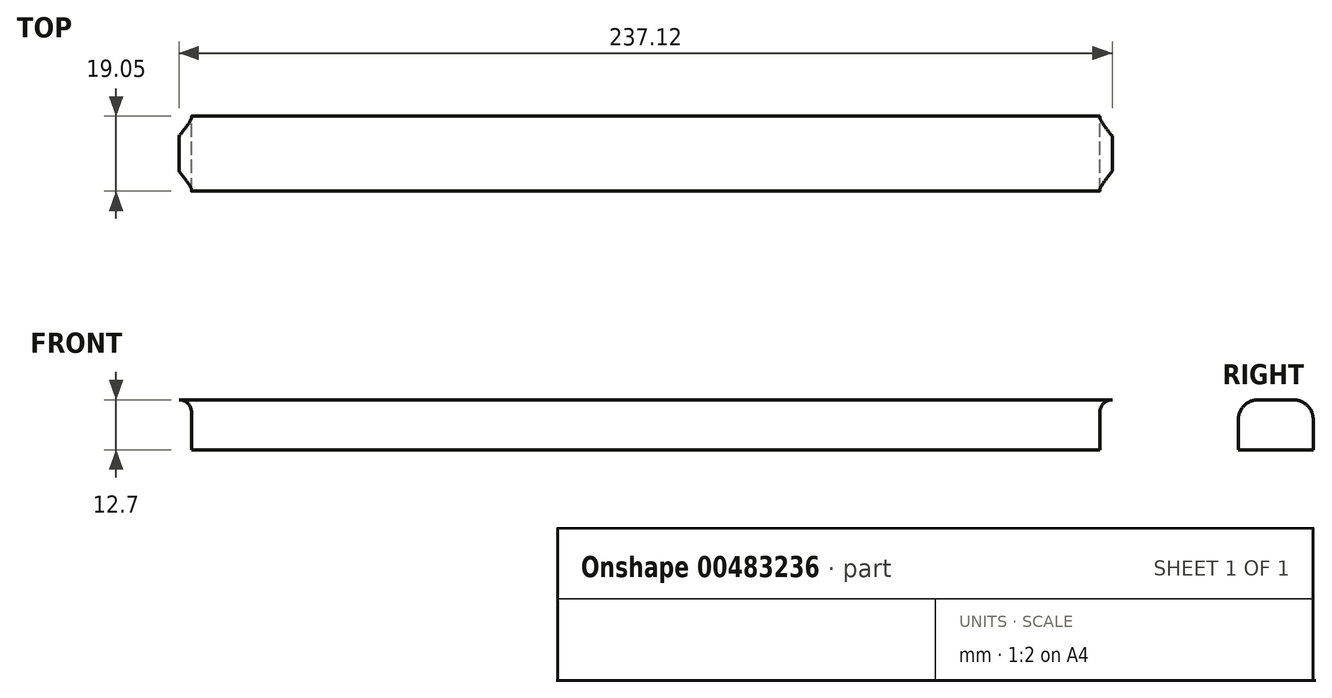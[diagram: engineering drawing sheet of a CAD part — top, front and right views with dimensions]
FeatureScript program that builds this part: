
annotation { "Feature Type Name" : "Feature", "Feature Type Description" : "" }
export const myFeature = defineFeature(function(context is Context, id is Id, definition is map)
    precondition{}
    {
        {
            var Q0;
            Q0=qCreatedBy(makeId("Front.planeOp"),FACE);
            var sketch = newSketch(context, id + "F0", { "sketchPlane" : qUnion([Q0])});
            skLineSegment(sketch, "E0.bottom", {"start": v(118.56, 6.35) * mm, "end": v(-118.56, 6.35) * mm});
            skLineSegment(sketch, "E0.top", {"start": v(115.39, -6.35) * mm, "end": v(-115.39, -6.35) * mm});
            skPoint(sketch, "E0.middle", {"position": v(0, 0) * mm});
            skLineSegment(sketch, "E1", {"start": v(-115.39, 3.18) * mm, "end": v(-115.39, -6.35) * mm});
            skLineSegment(sketch, "E2", {"start": v(115.39, 3.17) * mm, "end": v(115.39, -6.35) * mm});
            skArc(sketch, "E3", {"start": v(118.56, 6.35) * mm, "mid": v(116.32, 5.42) * mm, "end": v(115.39, 3.17) * mm});
            skPoint(sketch, "E4.orphan", {"position": v(118.56, -6.35) * mm});
            skArc(sketch, "E5", {"start": v(-115.39, 3.18) * mm, "mid": v(-116.32, 5.42) * mm, "end": v(-118.56, 6.35) * mm});
            skPoint(sketch, "E6.orphan", {"position": v(-118.56, -6.35) * mm});
            skSolve(sketch);
        }
        {
            var Q0;
            Q0 = qSketchRegion(id + "F0", true);
            extrude(context, id + "F1", {"entities" : qUnion([Q0]), "depth" : 19.05 * mm});
        }
        {
            var Q0;
            Q0=makeQuery(id+"F1.opExtrude","CAP_EDGE",EDGE,{"disambiguationData":[OSD([sQuery(id+"F0.wireOp",EDGE,"E0.bottom")])],"isStart":false});
            var Q1;
            Q1=makeQuery(id+"F1.opExtrude","CAP_EDGE",EDGE,{"disambiguationData":[OSD([sQuery(id+"F0.wireOp",EDGE,"E0.bottom")])],"isStart":true});
            fillet(context, id + "F2", {"entities" : qUnion([Q0, Q1]), "radius" : 5.08 * mm, "tangentPropagation" : true, "allowEdgeOverflow" : false});
        }
    });
